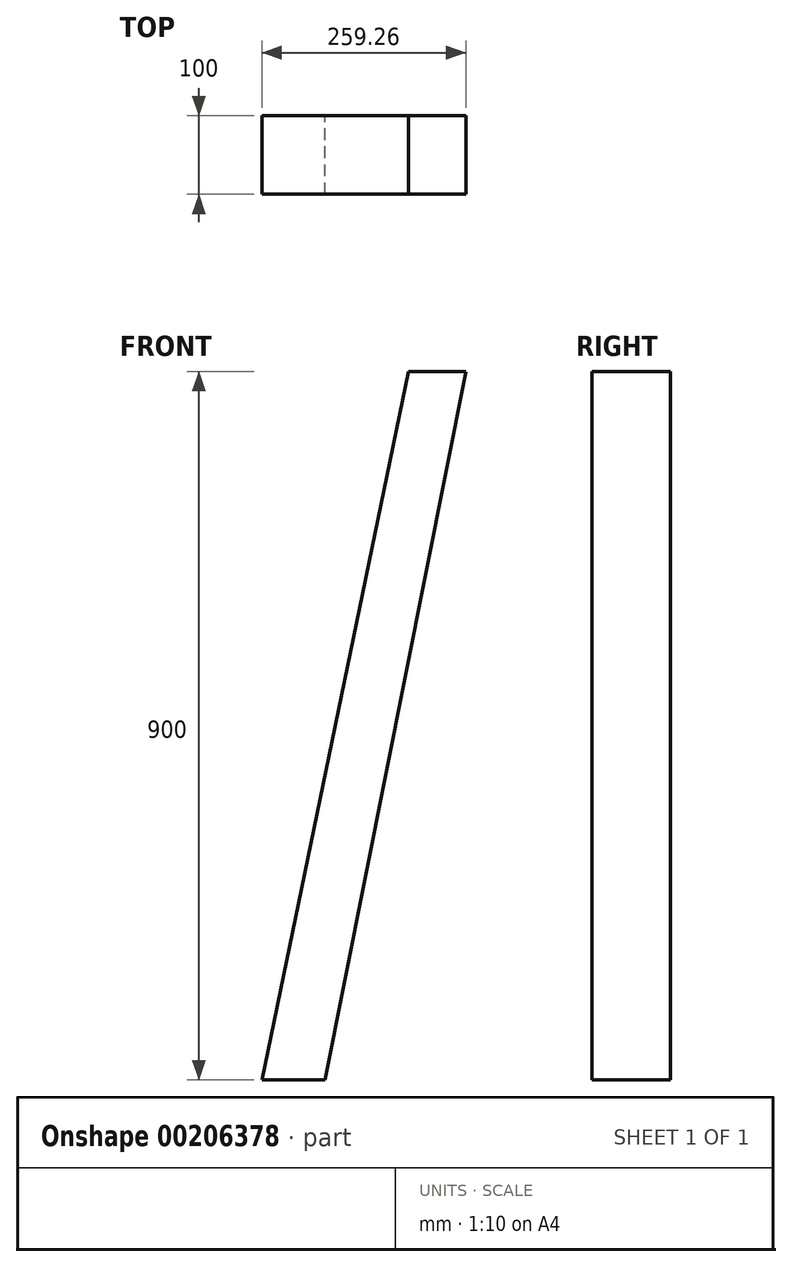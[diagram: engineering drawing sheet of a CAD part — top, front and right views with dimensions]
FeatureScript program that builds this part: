
annotation { "Feature Type Name" : "Feature", "Feature Type Description" : "" }
export const myFeature = defineFeature(function(context is Context, id is Id, definition is map)
    precondition{}
    {
        {
            var Q0;
            Q0=qCreatedBy(makeId("Front.planeOp"),FACE);
            var sketch = newSketch(context, id + "F0", { "sketchPlane" : qUnion([Q0])});
            skLineSegment(sketch, "E0", {"start": v(72.48, 613.5) * mm, "end": v(-0.37, 613.5) * mm});
            skLineSegment(sketch, "E1", {"start": v(-0.37, 613.5) * mm, "end": v(-186.78, -286.5) * mm});
            skLineSegment(sketch, "E2", {"start": v(-186.78, -286.5) * mm, "end": v(-106.78, -286.5) * mm});
            skLineSegment(sketch, "E3", {"start": v(-106.78, -286.5) * mm, "end": v(72.48, 613.5) * mm});
            skSolve(sketch);
        }
        {
            var Q0;
            Q0=makeQuery(id+"F0.imprint","IMPRINT",FACE,{"disambiguationData":[TD([[makeQuery(id+"F0.imprint","IMPRINT",EDGE,{"derivedFrom":sQuery(id+"F0.wireOp",EDGE,"E0")}),1.0]])]});
            extrude(context, id + "F1", {"entities" : qUnion([Q0]), "depth" : 100 * mm});
        }
    });
